# Revit family: DefaultType
name_source: partatom
category: Specialty Equipment
revit_build: Autodesk Revit 2018 (Build: 20180423_1000(x64)
units: mm (PartAtom-declared; Revit-internal decimal feet)

## family parameters
Always vertical = Yes
Cut with Voids When Loaded = No
OmniClass Number = 23.40.40.14.24
OmniClass Title = Food Dispensing Equipment
Part Type = Normal
Room Calculation Point = No
Round Connector Dimension = Use Diameter
Shared = No
Work Plane-Based = No

## types (1)
- DefaultType
    Assembly Code = E1090320
    CSI MasterFormat = 11 46 00
    Cold Water Connection Height = 1' - 9"
    Cold Water Flow = 0.528 GPM
    Cold Water Maximum Pressure = 100.00 psi
    Cold Water Minimum Pressure = 29.00 psi
    Cold Water RI Height = 0' - 0"
    Cold Water Size = 1"
    Cold Water Temperature Recommended = 40 °F
    Depth = 0' - 8 3/4"
    Description = Water Filter
    Foodservice Equipment Identifier = Yes
    Height = 1' - 8 15/32"
    Identify Quantity as Lot = Yes
    KCL SpecSheet URL = http://kclweb.kclcad.com
    KCLRef = KCL2C9,,78231ec1-364d-4268-80cb-1ddd86d2b1f2,VI,PURITY 600 QUELL ST,637475599480000000,8e114d0b-1a72-44e3-9316-f1a5b439c265,f091dbfa-86dd-40d3-9bec-e4dba1ab7b32
    Manufacturer = Vivreau
    Masterspec = Division 11
    Model = PURITY 600 Quell ST
    Plumbing Connection Type = NPT
    Specification by Manufacturer = Purity Quell ST 600 water filtration kit, includes 1 MDU filter head, vessel, filter cartridge. Capacity of 1940 gallons for coffee, espresso, vending.   Max operating pressure 100 psi, water intake temp 39-86 degrees Fahrenheit, Nominal flow 120 l/h.   Dimensions h/w  20.4/9.8in, weight dry/wet 26/33lbs, connection G1”, position horizontal and vertical.  Technology, decarbonization.  Systematic filter system, pre-filter, carbonate hardness reduction, activated carbon filtration and fine filtration.
    URL = www.vivreauwater.com/professional-filters
    URL Cutsheet = www.vivreauwater.com/purity_quell_st_spec-sheet_vivreau
    Weight in Pounds = 26
    Width = 0' - 9 13/16"

## geometry (parser evidence)
native form markers: Sweep x2
no freeform markers — native parametric forms only
